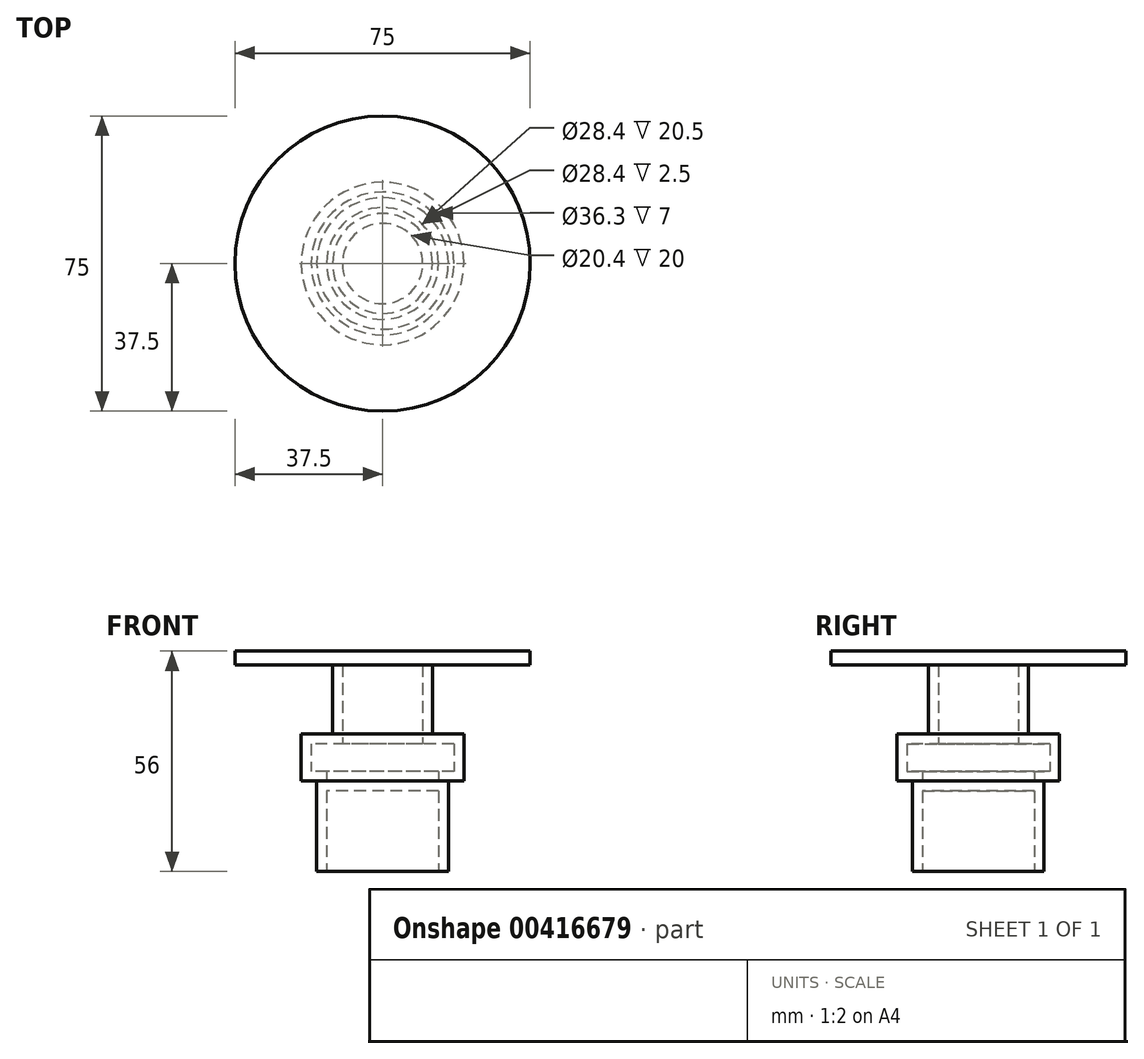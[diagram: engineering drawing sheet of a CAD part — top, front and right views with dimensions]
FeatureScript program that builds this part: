
annotation { "Feature Type Name" : "Feature", "Feature Type Description" : "" }
export const myFeature = defineFeature(function(context is Context, id is Id, definition is map)
    precondition{}
    {
        {
            var Q0;
            Q0=qCreatedBy(makeId("Top.planeOp"),FACE);
            var sketch = newSketch(context, id + "F0", { "sketchPlane" : qUnion([Q0])});
            skCircle(sketch, "E0", {"center": v(0, 0) * mm, "radius": 16.7 * mm});
            skSolve(sketch);
        }
        {
            var Q0;
            Q0=makeQuery(id+"F0.imprint","IMPRINT",FACE,{"disambiguationData":[TD([[makeQuery(id+"F0.imprint","IMPRINT",EDGE,{"derivedFrom":sQuery(id+"F0.wireOp",EDGE,"E0")}),1.0]])]});
            extrude(context, id + "F1", {"entities" : qUnion([Q0]), "depth" : 23 * mm});
        }
        {
            var Q0;
            Q0=makeQuery(id+"F1.opExtrude","CAP_FACE",FACE,{"disambiguationData":[OSD([sQuery(id+"F0.wireOp",EDGE,"E0")])],"isStart":true});
            shell(context, id + "F2", {"entities" : qUnion([Q0]), "thickness" : 2.5 * mm});
        }
        {
            var Q0;
            Q0=makeQuery(id+"F1.opExtrude","CAP_FACE",FACE,{"disambiguationData":[OSD([sQuery(id+"F0.wireOp",EDGE,"E0")])],"isStart":false});
            var sketch = newSketch(context, id + "F3", { "sketchPlane" : qUnion([Q0])});
            skCircle(sketch, "E1", {"center": v(0, 0) * mm, "radius": 20.65 * mm});
            skSolve(sketch);
        }
        {
            var Q0;
            Q0=makeQuery(id+"F3.imprint","IMPRINT",FACE,{"disambiguationData":[TD([[makeQuery(id+"F3.imprint","IMPRINT",EDGE,{"derivedFrom":sQuery(id+"F3.wireOp",EDGE,"E1")}),1.0]])]});
            var Q1;
            Q1=makeQuery(id+"F3.imprint","IMPRINT",FACE,{"disambiguationData":[TD([[makeQuery(id+"F3.imprint","IMPRINT",EDGE,{"derivedFrom":makeQuery(id+"F1.opExtrude","CAP_EDGE",EDGE,{"disambiguationData":[OSD([sQuery(id+"F0.wireOp",EDGE,"E0")])],"isStart":false})}),1.0]])]});
            extrude(context, id + "F4", {"entities" : qUnion([Q0, Q1]), "operationType" : NewBodyOperationType.ADD, "depth" : 12 * mm});
        }
        {
            var Q0;
            Q0=makeQuery(id+"F4.opExtrude","CAP_FACE",FACE,{"disambiguationData":[OSD([sQuery(id+"F3.wireOp",EDGE,"E1")])],"isStart":false});
            var sketch = newSketch(context, id + "F5", { "sketchPlane" : qUnion([Q0])});
            skCircle(sketch, "E2", {"center": v(0, 0) * mm, "radius": 12.7 * mm});
            skSolve(sketch);
        }
        {
            var Q0;
            Q0=makeQuery(id+"F5.imprint","IMPRINT",FACE,{"disambiguationData":[TD([[makeQuery(id+"F5.imprint","IMPRINT",EDGE,{"derivedFrom":sQuery(id+"F5.wireOp",EDGE,"E2")}),1.0]])]});
            extrude(context, id + "F6", {"entities" : qUnion([Q0]), "operationType" : NewBodyOperationType.ADD, "depth" : 17.5 * mm});
        }
        {
            var Q0;
            Q0=makeQuery(id+"F6.opExtrude","CAP_FACE",FACE,{"disambiguationData":[OSD([sQuery(id+"F5.wireOp",EDGE,"E2")])],"isStart":false});
            shell(context, id + "F7", {"entities" : qUnion([Q0]), "thickness" : 2.5 * mm});
        }
        {
            var Q0;
            Q0=makeQuery(id+"F6.opExtrude","CAP_FACE",FACE,{"disambiguationData":[OSD([sQuery(id+"F5.wireOp",EDGE,"E2")])],"isStart":false});
            var sketch = newSketch(context, id + "F8", { "sketchPlane" : qUnion([Q0])});
            skCircle(sketch, "E3", {"center": v(0, 0) * mm, "radius": 37.5 * mm});
            skSolve(sketch);
        }
        {
            var Q0;
            Q0=makeQuery(id+"F8.imprint","IMPRINT",FACE,{"disambiguationData":[TD([[makeQuery(id+"F8.imprint","IMPRINT",EDGE,{"derivedFrom":sQuery(id+"F8.wireOp",EDGE,"E3")}),1.0]])]});
            var Q1;
            {var subQ0=sQuery(id+"F5.wireOp",EDGE,"E2");var subQ1=makeQuery(id+"F6.opExtrude","CAP_EDGE",EDGE,{"disambiguationData":[OSD([subQ0])],"isStart":false});Q1=makeQuery(id+"F8.imprint","IMPRINT",FACE,{"disambiguationData":[TD([[makeQuery(id+"F8.imprint","IMPRINT",EDGE,{"derivedFrom":subQ1}),1.0]])]});}
            var Q2;
            {var subQ0=sQuery(id+"F5.wireOp",EDGE,"E2");Q2=makeQuery(id+"F8.imprint","IMPRINT",FACE,{"disambiguationData":[TD([[makeQuery(id+"F8.imprint","IMPRINT",EDGE,{"derivedFrom":makeQuery(id+"F7.opShell","OFFSET_EDGE",EDGE,{"disambiguationData":[OSD([subQ0]),TDD([makeQuery(id+"F6.opExtrude","CAP_EDGE",EDGE,{"disambiguationData":[OSD([subQ0])],"isStart":false})])]})}),1.0]])]});}
            extrude(context, id + "F9", {"entities" : qUnion([Q0, Q1, Q2]), "operationType" : NewBodyOperationType.ADD, "depth" : 3.5 * mm});
        }
    });
